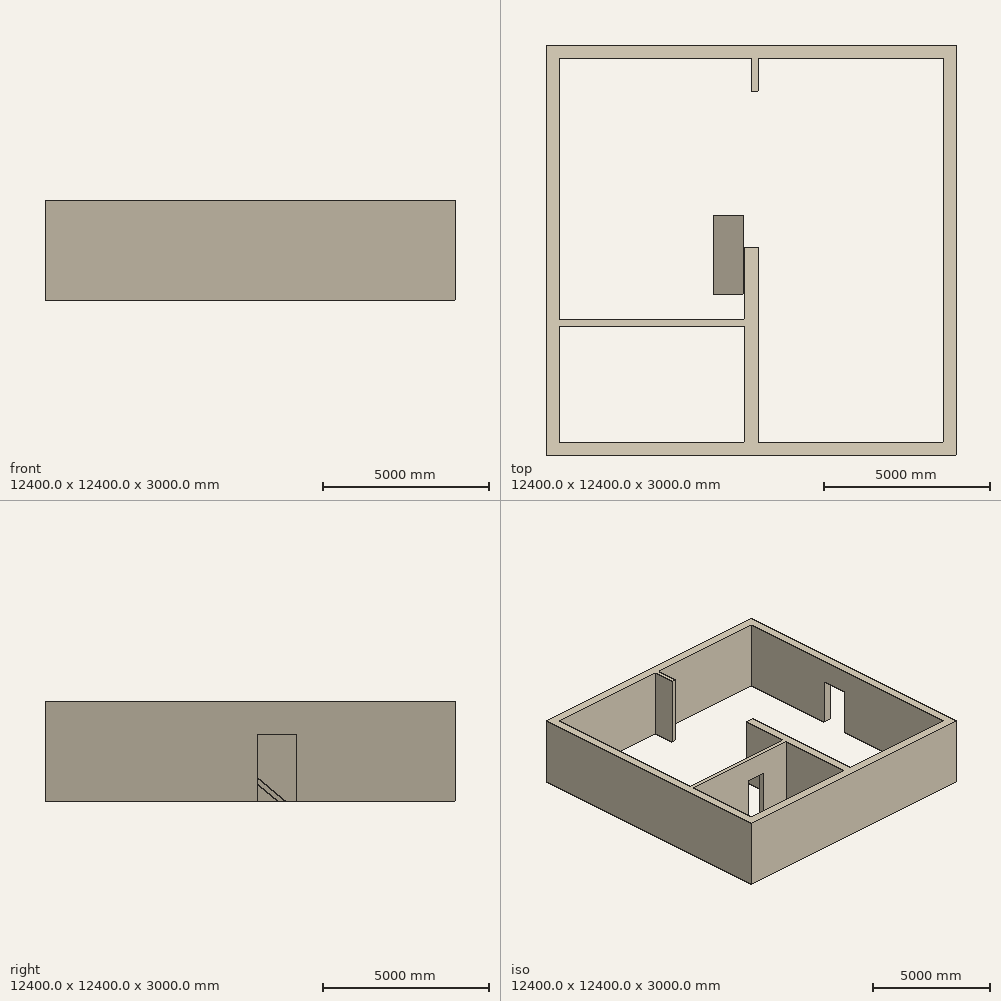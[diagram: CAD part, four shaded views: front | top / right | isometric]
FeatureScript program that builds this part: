
annotation { "Feature Type Name" : "Feature", "Feature Type Description" : "" }
export const myFeature = defineFeature(function(context is Context, id is Id, definition is map)
    precondition{}
    {
        {
            var Q0;
            Q0=qCreatedBy(makeId("Top.planeOp"),FACE);
            var sketch = newSketch(context, id + "F0", { "sketchPlane" : qUnion([Q0])});
            skLineSegment(sketch, "E0.bottom", {"start": v(12400, 0) * mm, "end": v(0, 0) * mm});
            skLineSegment(sketch, "E0.top", {"start": v(12400, 12400) * mm, "end": v(0, 12400) * mm});
            skLineSegment(sketch, "E0.left", {"start": v(12400, 0) * mm, "end": v(12400, 12400) * mm});
            skLineSegment(sketch, "E0.right", {"start": v(0, 0) * mm, "end": v(0, 12400) * mm});
            skLineSegment(sketch, "E1.bottom", {"start": v(400, 400) * mm, "end": v(6000, 400) * mm});
            skLineSegment(sketch, "E1.top", {"start": v(400, 12000) * mm, "end": v(6000, 12000) * mm});
            skLineSegment(sketch, "E1.left", {"start": v(400, 400) * mm, "end": v(400, 12000) * mm});
            skLineSegment(sketch, "E1.right", {"start": v(6000, 400) * mm, "end": v(6000, 6300) * mm});
            skLineSegment(sketch, "E2.bottom", {"start": v(6400, 400) * mm, "end": v(12000, 400) * mm});
            skLineSegment(sketch, "E2.top", {"start": v(6400, 12000) * mm, "end": v(12000, 12000) * mm});
            skLineSegment(sketch, "E2.left", {"start": v(6400, 400) * mm, "end": v(6400, 6300) * mm});
            skLineSegment(sketch, "E2.right", {"start": v(12000, 400) * mm, "end": v(12000, 12000) * mm});
            skLineSegment(sketch, "E3", {"start": v(7600, 8000) * mm, "end": v(12000, 8000) * mm});
            skLineSegment(sketch, "E4", {"start": v(12000, 7800) * mm, "end": v(9500, 7800) * mm});
            skLineSegment(sketch, "E5", {"start": v(9500, 7800) * mm, "end": v(9500, 5300) * mm});
            skLineSegment(sketch, "E6", {"start": v(9500, 5300) * mm, "end": v(12000, 5300) * mm});
            skLineSegment(sketch, "E7", {"start": v(12000, 5100) * mm, "end": v(9300, 5100) * mm});
            skLineSegment(sketch, "E8", {"start": v(9300, 5100) * mm, "end": v(9300, 7800) * mm});
            skLineSegment(sketch, "E9", {"start": v(9300, 7800) * mm, "end": v(7517.16, 7800) * mm});
            skLineSegment(sketch, "E10", {"start": v(400, 3900) * mm, "end": v(6000, 3900) * mm});
            skLineSegment(sketch, "E11", {"start": v(400, 4100) * mm, "end": v(6000, 4100) * mm});
            skLineSegment(sketch, "E12", {"start": v(400, 7700) * mm, "end": v(3400, 7700) * mm});
            skLineSegment(sketch, "E13", {"start": v(3400, 7700) * mm, "end": v(3400, 4100) * mm});
            skLineSegment(sketch, "E14", {"start": v(3600, 7900) * mm, "end": v(400, 7900) * mm});
            skLineSegment(sketch, "E15", {"start": v(3600, 7617.16) * mm, "end": v(3600, 4100) * mm});
            skLineSegment(sketch, "E16.bottom", {"start": v(5050, 7250) * mm, "end": v(5950, 7250) * mm, "construction": true});
            skLineSegment(sketch, "E16.top", {"start": v(5050, 3250) * mm, "end": v(5950, 3250) * mm, "construction": true});
            skLineSegment(sketch, "E16.left", {"start": v(5050, 7250) * mm, "end": v(5050, 3250) * mm, "construction": true});
            skLineSegment(sketch, "E16.right", {"start": v(5950, 7250) * mm, "end": v(5950, 3250) * mm, "construction": true});
            skLineSegment(sketch, "E17", {"start": v(4782.84, 8800) * mm, "end": v(6517.16, 8800) * mm});
            skLineSegment(sketch, "E18", {"start": v(6517.16, 8800) * mm, "end": v(7517.16, 7800) * mm});
            skLineSegment(sketch, "E19", {"start": v(7600, 8000) * mm, "end": v(6600, 9000) * mm});
            skLineSegment(sketch, "E20", {"start": v(6600, 9000) * mm, "end": v(6400, 9000) * mm});
            skLineSegment(sketch, "E21.trimOffspring", {"start": v(4700, 9000) * mm, "end": v(4700, 12000) * mm});
            skLineSegment(sketch, "E22", {"start": v(6000, 12000) * mm, "end": v(6200, 12000) * mm});
            skLineSegment(sketch, "E23", {"start": v(6200, 12000) * mm, "end": v(6200, 11000) * mm});
            skLineSegment(sketch, "E24", {"start": v(6400, 12000) * mm, "end": v(6400, 11000) * mm});
            skLineSegment(sketch, "E25", {"start": v(6400, 11000) * mm, "end": v(6200, 11000) * mm});
            skLineSegment(sketch, "E26", {"start": v(6200, 9200) * mm, "end": v(6200, 10100) * mm});
            skLineSegment(sketch, "E27", {"start": v(6200, 10100) * mm, "end": v(6400, 10100) * mm});
            skLineSegment(sketch, "E28", {"start": v(6400, 10100) * mm, "end": v(6400, 9000) * mm});
            skLineSegment(sketch, "E29", {"start": v(4782.84, 8800) * mm, "end": v(3600, 7617.16) * mm});
            skLineSegment(sketch, "E30", {"start": v(4500, 8800) * mm, "end": v(3600, 7900) * mm});
            skLineSegment(sketch, "E31.trimOffspring", {"start": v(4500, 8800) * mm, "end": v(4500, 12000) * mm});
            skLineSegment(sketch, "E32.trimOffspring", {"start": v(6000, 9000) * mm, "end": v(4700, 9000) * mm});
            skLineSegment(sketch, "E33", {"start": v(6000, 6300) * mm, "end": v(6400, 6300) * mm});
            skLineSegment(sketch, "E34", {"start": v(6200, 9200) * mm, "end": v(6000, 9200) * mm});
            skLineSegment(sketch, "E35", {"start": v(6000, 9200) * mm, "end": v(6000, 9000) * mm});
            skLineSegment(sketch, "E36", {"start": v(5950, 7250) * mm, "end": v(6650, 7250) * mm, "construction": true});
            skLineSegment(sketch, "E37", {"start": v(6650, 7250) * mm, "end": v(6650, 6350) * mm, "construction": true});
            skLineSegment(sketch, "E38", {"start": v(6650, 6350) * mm, "end": v(5950, 6350) * mm, "construction": true});
            skSolve(sketch);
        }
        {
            var Q0;
            Q0=makeQuery(id+"F0.imprint","IMPRINT",FACE,{"disambiguationData":[TD([[makeQuery(id+"F0.imprint","IMPRINT",EDGE,{"derivedFrom":sQuery(id+"F0.wireOp",EDGE,"E0.bottom")}),-1.0]])]});
            var Q1;
            {var subQ1=sQuery(id+"F0.wireOp",EDGE,"E12");Q1=makeQuery(id+"F0.imprint","IMPRINT",FACE,{"disambiguationData":[TD([[makeQuery(id+"F0.imprint","IMPRINT",EDGE,{"derivedFrom":subQ1}),1.0]])]});}
            var Q2;
            {var subQ4=sQuery(id+"F0.wireOp",EDGE,"E10");Q2=makeQuery(id+"F0.imprint","IMPRINT",FACE,{"disambiguationData":[TD([[makeQuery(id+"F0.imprint","IMPRINT",EDGE,{"derivedFrom":subQ4}),1.0]])]});}
            var Q3;
            {var subQ0=sQuery(id+"F0.wireOp",EDGE,"kvUPGbzR-Rbo3-Q6iu-vvTJ-yD9WQZE7Eaqy");Q3=makeQuery(id+"F0.imprint","IMPRINT",FACE,{"disambiguationData":[TD([[makeQuery(id+"F0.imprint","IMPRINT",EDGE,{"derivedFrom":subQ0}),-1.0]])]});}
            var Q4;
            {var subQ1=sQuery(id+"F0.wireOp",EDGE,"MLB5zXMS-D5Dv-TWFG-MVfa-ymxDCrCVvkNw");Q4=makeQuery(id+"F0.imprint","IMPRINT",FACE,{"disambiguationData":[TD([[makeQuery(id+"F0.imprint","IMPRINT",EDGE,{"derivedFrom":subQ1}),-1.0]])]});}
            var Q5;
            {var subQ0=sQuery(id+"F0.wireOp",EDGE,"E3");Q5=makeQuery(id+"F0.imprint","IMPRINT",FACE,{"disambiguationData":[TD([[makeQuery(id+"F0.imprint","IMPRINT",EDGE,{"derivedFrom":subQ0}),-1.0]])]});}
            extrude(context, id + "F1", {"entities" : qUnion([Q0, Q1, Q2, Q3, Q4, Q5]), "depth" : 3000 * mm, "offsetDistance" : 25 * mm});
        }
        {
            var Q0;
            Q0=makeQuery(id+"F1.opExtrude","SWEPT_FACE",FACE,{"disambiguationData":[OSD([sQuery(id+"F0.wireOp",EDGE,"E0.left")])]});
            var sketch = newSketch(context, id + "F2", { "sketchPlane" : qUnion([Q0])});
            skLineSegment(sketch, "E39.0", {"start": v(7800, 3000) * mm, "end": v(7800, 0) * mm});
            skLineSegment(sketch, "E40.0", {"start": v(5300, 3000) * mm, "end": v(5300, 0) * mm});
            skLineSegment(sketch, "E41.bottom", {"start": v(7600, 0) * mm, "end": v(6400, 0) * mm});
            skLineSegment(sketch, "E41.top", {"start": v(7600, 2000) * mm, "end": v(6400, 2000) * mm});
            skLineSegment(sketch, "E41.left", {"start": v(7600, 0) * mm, "end": v(7600, 2000) * mm});
            skLineSegment(sketch, "E41.right", {"start": v(6400, 0) * mm, "end": v(6400, 2000) * mm});
            skSolve(sketch);
        }
        {
            var Q0;
            Q0=makeQuery(id+"F2.imprint","IMPRINT",FACE,{"disambiguationData":[TD([[makeQuery(id+"F2.imprint","IMPRINT",EDGE,{"derivedFrom":sQuery(id+"F2.wireOp",EDGE,"E41.bottom")}),1.0]])]});
            var Q1;
            {var subQ0=sQuery(id+"F0.wireOp",EDGE,"E2.left");Q1=makeQuery(id+"F1.opExtrude","SWEPT_FACE",FACE,{"disambiguationData":[OSD([subQ0]),TDD([makeQuery(id+"F0.imprint","IMPRINT",EDGE,{"disambiguationData":[TD([[makeQuery(id+"F0.imprint","INTERSECT",VERTEX,{"derivedFrom":[sQuery(id+"F0.wireOp",EDGE,"E2.bottom"),subQ0]}),-1.0]])],"derivedFrom":subQ0})])]});}
            extrude(context, id + "F3", {"entities" : qUnion([Q0]), "operationType" : NewBodyOperationType.REMOVE, "endBound" : BoundingType.UP_TO_SURFACE, "oppositeDirection" : true, "depth" : 25 * mm, "endBoundEntityFace" : qUnion([Q1]), "offsetDistance" : 25 * mm});
        }
        {
            var Q0;
            {var subQ0=sQuery(id+"F0.wireOp",EDGE,"E2.left");Q0=makeQuery(id+"F1.opExtrude","SWEPT_FACE",FACE,{"disambiguationData":[OSD([subQ0]),TDD([makeQuery(id+"F0.imprint","IMPRINT",EDGE,{"disambiguationData":[TD([[makeQuery(id+"F0.imprint","INTERSECT",VERTEX,{"derivedFrom":[sQuery(id+"F0.wireOp",EDGE,"E2.bottom"),subQ0]}),-1.0]])],"derivedFrom":subQ0})])]});}
            var sketch = newSketch(context, id + "F4", { "sketchPlane" : qUnion([Q0])});
            skLineSegment(sketch, "E42.0", {"start": v(7600, 0) * mm, "end": v(7600, 2000) * mm});
            skLineSegment(sketch, "E43", {"start": v(7600, 0) * mm, "end": v(5600, 0) * mm});
            skLineSegment(sketch, "E44", {"start": v(5600, 0) * mm, "end": v(5600, 2000) * mm});
            skLineSegment(sketch, "E45", {"start": v(5600, 2000) * mm, "end": v(7600, 2000) * mm});
            skSolve(sketch);
        }
        {
            var Q0;
            Q0=makeQuery(id+"F4.imprint","IMPRINT",FACE,{"disambiguationData":[TD([[makeQuery(id+"F4.imprint","IMPRINT",EDGE,{"derivedFrom":sQuery(id+"F4.wireOp",EDGE,"E42.0")}),1.0]])]});
            extrude(context, id + "F5", {"entities" : qUnion([Q0]), "operationType" : NewBodyOperationType.REMOVE, "endBound" : BoundingType.UP_TO_NEXT, "oppositeDirection" : true, "depth" : 25 * mm, "offsetDistance" : 25 * mm});
        }
        {
            var Q0;
            {var subQ0=sQuery(id+"F0.wireOp",EDGE,"E11");Q0=makeQuery(id+"F1.opExtrude","SWEPT_FACE",FACE,{"disambiguationData":[OSD([subQ0]),TDD([makeQuery(id+"F0.imprint","IMPRINT",EDGE,{"disambiguationData":[TD([[makeQuery(id+"F0.imprint","INTERSECT",VERTEX,{"derivedFrom":[sQuery(id+"F0.wireOp",EDGE,"E1.right"),subQ0]}),1.0]])],"derivedFrom":subQ0})])]});}
            var sketch = newSketch(context, id + "F6", { "sketchPlane" : qUnion([Q0])});
            skLineSegment(sketch, "E46.bottom", {"start": v(-3700, 0) * mm, "end": v(-4600, 0) * mm});
            skLineSegment(sketch, "E46.top", {"start": v(-3700, 2000) * mm, "end": v(-4600, 2000) * mm});
            skLineSegment(sketch, "E46.left", {"start": v(-3700, 0) * mm, "end": v(-3700, 2000) * mm});
            skLineSegment(sketch, "E46.right", {"start": v(-4600, 0) * mm, "end": v(-4600, 2000) * mm});
            skSolve(sketch);
        }
        {
            var Q0;
            Q0=makeQuery(id+"F6.imprint","IMPRINT",FACE,{"disambiguationData":[TD([[makeQuery(id+"F6.imprint","IMPRINT",EDGE,{"derivedFrom":sQuery(id+"F6.wireOp",EDGE,"E46.bottom")}),-1.0]])]});
            extrude(context, id + "F7", {"entities" : qUnion([Q0]), "operationType" : NewBodyOperationType.REMOVE, "endBound" : BoundingType.UP_TO_NEXT, "oppositeDirection" : true, "depth" : 25 * mm, "offsetDistance" : 25 * mm});
        }
        {
            var Q0;
            {var subQ0=sQuery(id+"F0.wireOp",EDGE,"E1.right");Q0=makeQuery(id+"F1.opExtrude","SWEPT_FACE",FACE,{"disambiguationData":[OSD([subQ0]),TDD([makeQuery(id+"F0.imprint","IMPRINT",EDGE,{"disambiguationData":[TD([[makeQuery(id+"F0.imprint","INTERSECT",VERTEX,{"derivedFrom":[subQ0,sQuery(id+"F0.wireOp",EDGE,"E11")]}),-1.0]])],"derivedFrom":subQ0})])]});}
            var Q1;
            Q1=sQuery(id+"F0.wireOp",VERTEX,"E16.bottom.end");
            cPlane(context, id + "F8", {"entities" : qUnion([Q0, Q1]), "cplaneType" : CPlaneType.PLANE_POINT, "offset" : 25 * mm, "width" : 150 * mm, "height" : 150 * mm});
        }
        {
            var Q0;
            Q0=qCreatedBy(id+"F8.planeOp",FACE);
            var sketch = newSketch(context, id + "F9", { "sketchPlane" : qUnion([Q0])});
            skPoint(sketch, "E47.0", {"position": v(-7250, 0) * mm});
            skLineSegment(sketch, "E48", {"start": v(-7250, 0) * mm, "end": v(-4866.5, 2000) * mm});
            skLineSegment(sketch, "E49", {"start": v(-4866.5, 2000) * mm, "end": v(-4866.5, 1804.19) * mm});
            skLineSegment(sketch, "E50", {"start": v(-4866.5, 1804.19) * mm, "end": v(-7016.64, 0) * mm});
            skLineSegment(sketch, "E51", {"start": v(-7016.64, 0) * mm, "end": v(-7250, 0) * mm});
            skSolve(sketch);
        }
        {
            var Q0;
            Q0=makeQuery(id+"F9.imprint","IMPRINT",FACE,{"disambiguationData":[TD([[makeQuery(id+"F9.imprint","IMPRINT",EDGE,{"derivedFrom":sQuery(id+"F9.wireOp",EDGE,"E48")}),-1.0]])]});
            extrude(context, id + "F10", {"entities" : qUnion([Q0]), "operationType" : NewBodyOperationType.ADD, "depth" : 900 * mm, "offsetDistance" : 25 * mm});
        }
    });
